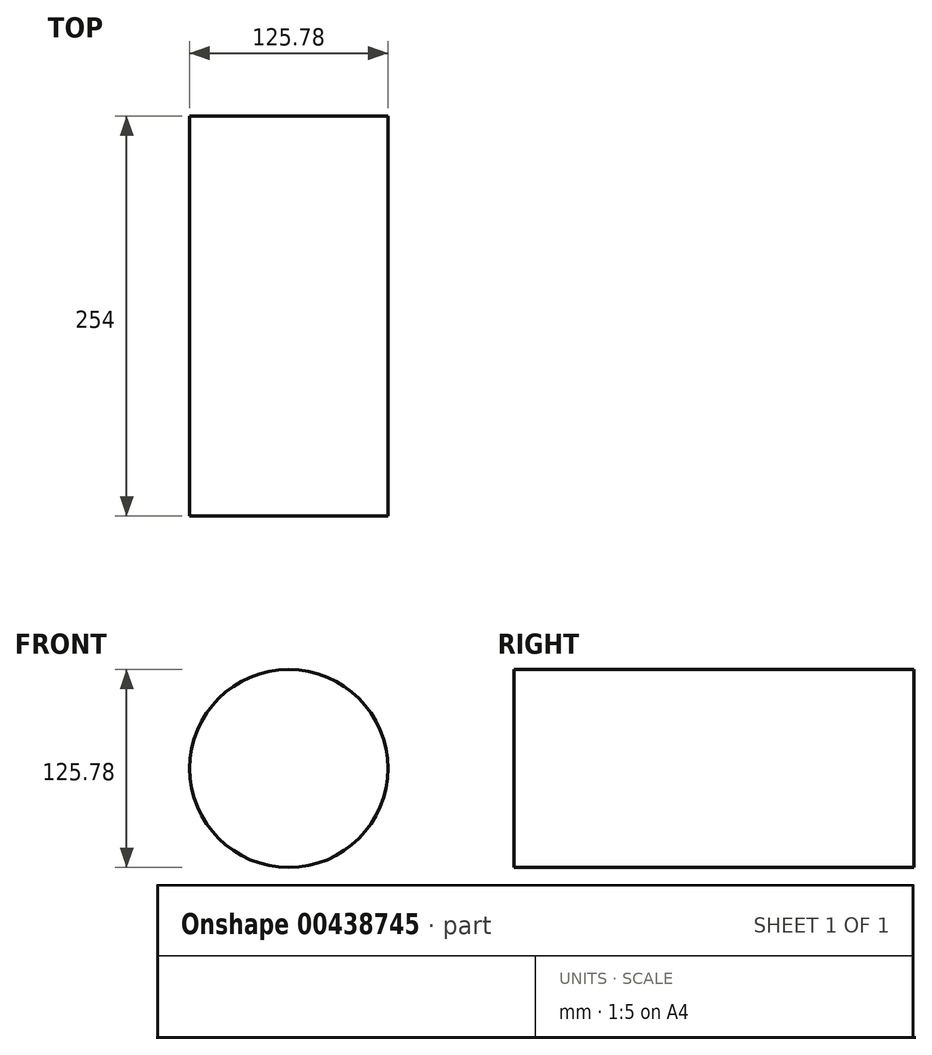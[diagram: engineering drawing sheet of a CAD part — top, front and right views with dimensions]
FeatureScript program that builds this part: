
annotation { "Feature Type Name" : "Feature", "Feature Type Description" : "" }
export const myFeature = defineFeature(function(context is Context, id is Id, definition is map)
    precondition{}
    {
        {
            var Q0;
            Q0=qCreatedBy(makeId("Front.planeOp"),FACE);
            var sketch = newSketch(context, id + "F0", { "sketchPlane" : qUnion([Q0])});
            skCircle(sketch, "E0", {"center": v(0, 0) * mm, "radius": 62.89 * mm});
            skSolve(sketch);
        }
        {
            var Q0;
            Q0=makeQuery(id+"F0.imprint","IMPRINT",FACE,{"disambiguationData":[TD([[makeQuery(id+"F0.imprint","IMPRINT",EDGE,{"derivedFrom":sQuery(id+"F0.wireOp",EDGE,"E0")}),1.0]])]});
            extrude(context, id + "F1", {"entities" : qUnion([Q0]), "depth" : 254 * mm});
        }
    });
